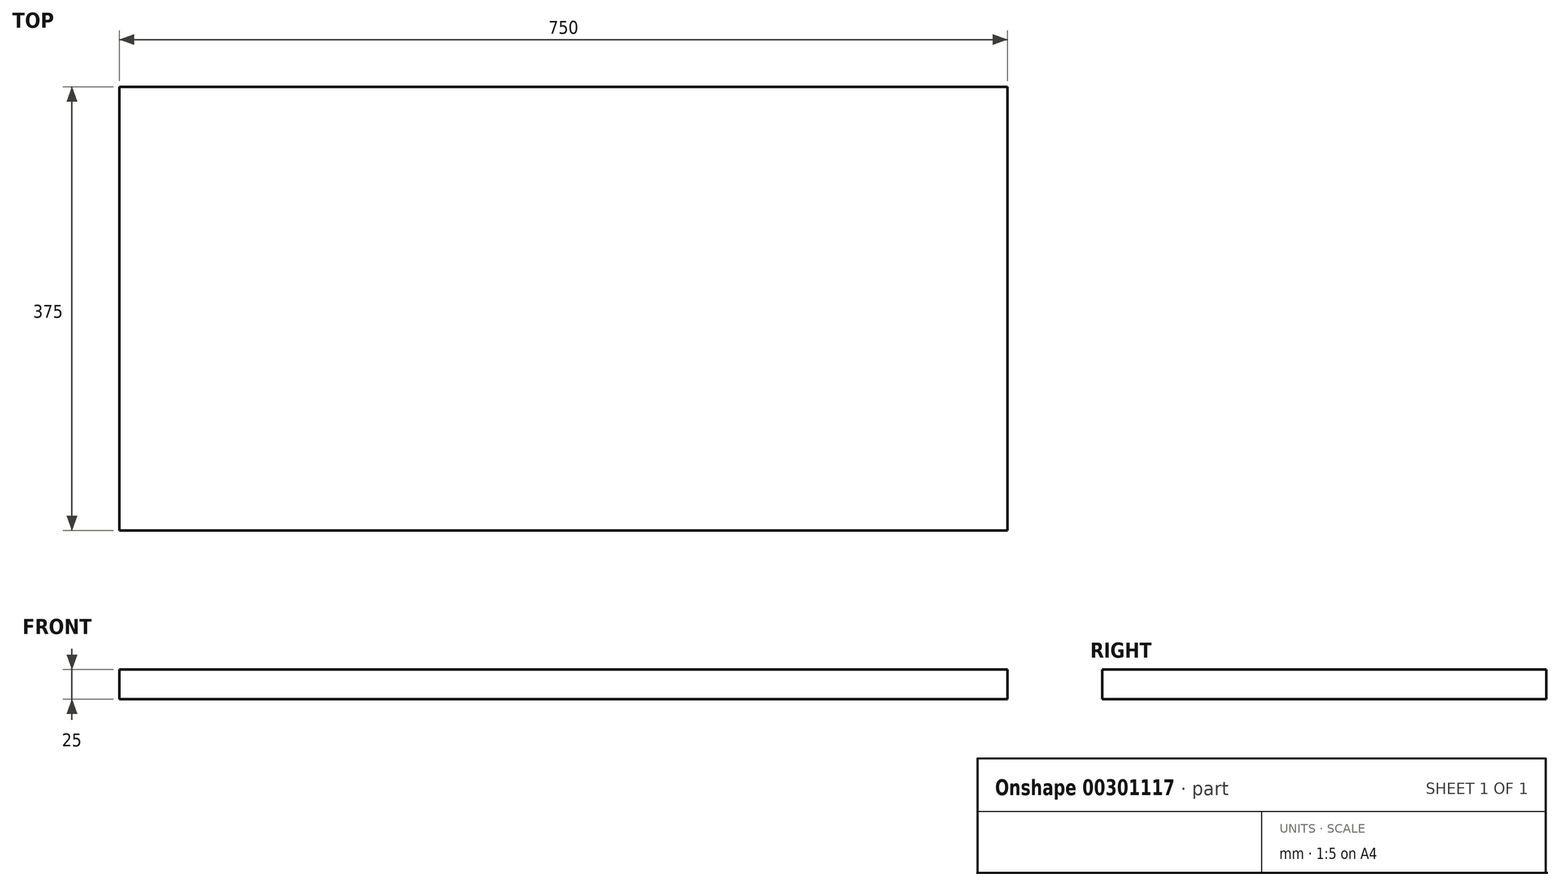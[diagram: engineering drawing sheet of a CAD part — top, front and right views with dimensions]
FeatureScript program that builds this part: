
annotation { "Feature Type Name" : "Feature", "Feature Type Description" : "" }
export const myFeature = defineFeature(function(context is Context, id is Id, definition is map)
    precondition{}
    {
        {
            var Q0;
            Q0=qCreatedBy(makeId("Top.planeOp"),FACE);
            var sketch = newSketch(context, id + "F0", { "sketchPlane" : qUnion([Q0])});
            skLineSegment(sketch, "E0.bottom", {"start": v(0, 0) * mm, "end": v(1500, 0) * mm});
            skLineSegment(sketch, "E0.top", {"start": v(0, -750) * mm, "end": v(1500, -750) * mm});
            skLineSegment(sketch, "E0.left", {"start": v(0, 0) * mm, "end": v(0, -750) * mm});
            skLineSegment(sketch, "E0.right", {"start": v(1500, 0) * mm, "end": v(1500, -750) * mm});
            skSolve(sketch);
        }
        {
            var Q0;
            Q0=qSketchRegion(id+"F0",true);
            extrude(context, id + "F1", {"entities" : qUnion([Q0]), "depth" : 50 * mm});
        }
        {
            var Q0;
            Q0=makeQuery(id+"F1.opExtrude","SWEPT_BODY",BODY,{"disambiguationData":[OSD([sQuery(id+"F0.wireOp",EDGE,"E0.bottom"),sQuery(id+"F0.wireOp",EDGE,"E0.top"),sQuery(id+"F0.wireOp",EDGE,"E0.left"),sQuery(id+"F0.wireOp",EDGE,"E0.right")])]});
            var Q1;
            Q1=qCreatedBy(makeId("Origin.pointOp"),VERTEX);
            var Q2;
            Q2=qCreatedBy(makeId("Origin.pointOp"),VERTEX);
            transform(context, id + "F2", {"entities" : qUnion([Q0]), "transformType" : TransformType.SCALE_UNIFORMLY, "scale" : 0.5, "scalePoint" : qUnion([Q2]), "makeCopy" : false});
        }
    });
